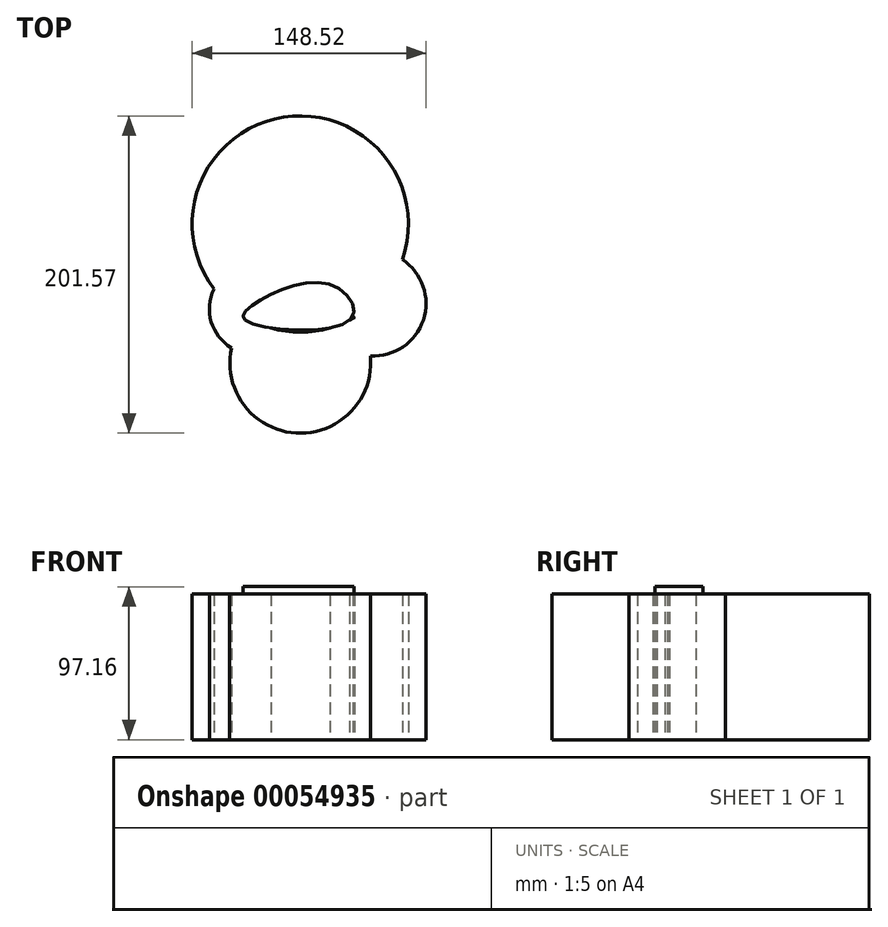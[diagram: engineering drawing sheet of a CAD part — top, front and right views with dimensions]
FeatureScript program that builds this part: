
annotation { "Feature Type Name" : "Feature", "Feature Type Description" : "" }
export const myFeature = defineFeature(function(context is Context, id is Id, definition is map)
    precondition{}
    {
        {
            var Q0;
            Q0=qCreatedBy(makeId("Top.planeOp"),FACE);
            var sketch = newSketch(context, id + "F1", { "sketchPlane" : qUnion([Q0])});
            skCircle(sketch, "E0", {"center": v(46.54, 0) * mm, "radius": 33.3 * mm});
            skCircle(sketch, "E1", {"center": v(0, -37.62) * mm, "radius": 44.75 * mm});
            skCircle(sketch, "E2", {"center": v(-28.77, -3.34) * mm, "radius": 28.96 * mm});
            skCircle(sketch, "E3", {"center": v(0, 50.52) * mm, "radius": 68.68 * mm});
            skSolve(sketch);
        }
        {
            var Q0;
            Q0 = qSketchRegion(id + "F1", true);
            extrude(context, id + "F2", {"entities" : qUnion([Q0]), "depth" : 92.52 * mm});
        }
        {
            var Q0;
            Q0=qCreatedBy(makeId("Top.planeOp"),FACE);
            var sketch = newSketch(context, id + "F3", { "sketchPlane" : qUnion([Q0])});
            skFitSpline(sketch, "E4", {"points": [v(-34.99, -10.6) * mm, v(-28.6, 0) * mm, v(20.15, 11.74) * mm, v(31.69, -10.24) * mm, v(-34.99, -10.6) * mm]});
            skSolve(sketch);
        }
        {
            var Q0;
            Q0 = qSketchRegion(id + "F3", true);
            extrude(context, id + "F0", {"entities" : qUnion([Q0]), "operationType" : NewBodyOperationType.ADD, "depth" : 97.16 * mm});
        }
    });
